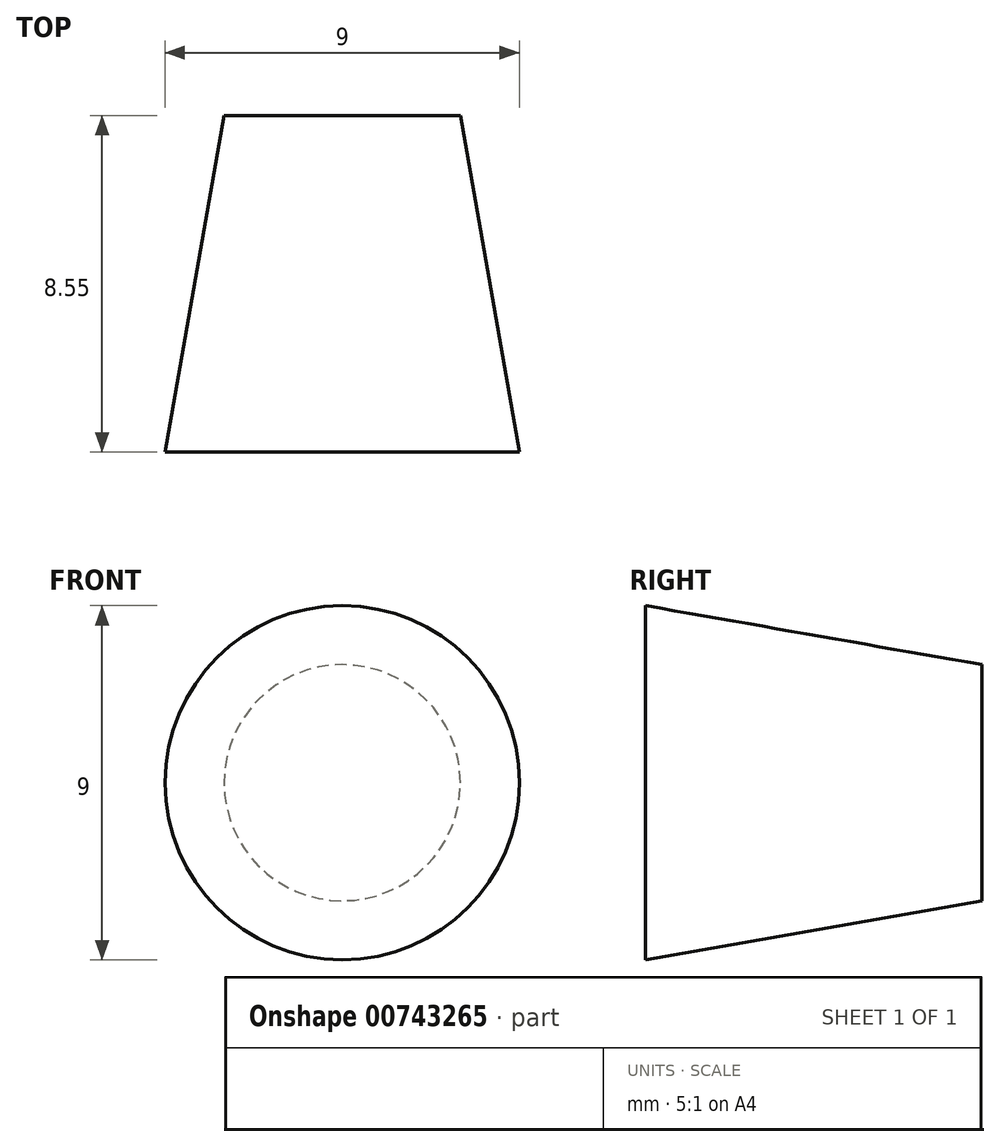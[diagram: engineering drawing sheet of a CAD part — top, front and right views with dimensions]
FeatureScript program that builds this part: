
annotation { "Feature Type Name" : "Feature", "Feature Type Description" : "" }
export const myFeature = defineFeature(function(context is Context, id is Id, definition is map)
    precondition{}
    {
        {
            var Q0;
            Q0=qCreatedBy(makeId("Top.planeOp"),FACE);
            var sketch = newSketch(context, id + "F0", { "sketchPlane" : qUnion([Q0])});
            skLineSegment(sketch, "E0", {"start": v(0, 0) * mm, "end": v(-4.5, 0) * mm});
            skLineSegment(sketch, "E1", {"start": v(-3, 8.55) * mm, "end": v(-4.5, 0) * mm});
            skLineSegment(sketch, "E2", {"start": v(0, 8.55) * mm, "end": v(0, 0) * mm});
            skLineSegment(sketch, "E3", {"start": v(-3, 8.55) * mm, "end": v(0, 8.55) * mm});
            skSolve(sketch);
        }
        {
            var Q0;
            Q0=qCreatedBy(makeId("Front.planeOp"),FACE);
            var sketch = newSketch(context, id + "F1", { "sketchPlane" : qUnion([Q0])});
            skCircle(sketch, "E4", {"center": v(0, 0) * mm, "radius": 8 * mm});
            skSolve(sketch);
        }
        {
            var Q0;
            Q0=makeQuery(id+"F0.imprint","IMPRINT",FACE,{"disambiguationData":[TD([[makeQuery(id+"F0.imprint","IMPRINT",EDGE,{"derivedFrom":sQuery(id+"F0.wireOp",EDGE,"E0")}),-1.0]])]});
            var Q1;
            Q1=sQuery(id+"F1.wireOp",EDGE,"E4");
            revolve(context, id + "F2", {"surfaceOperationType" : NewSurfaceOperationType.NEW, "entities" : qUnion([Q0]), "axis" : qUnion([Q1]), "revolveType" : RevolveType.FULL});
        }
    });
